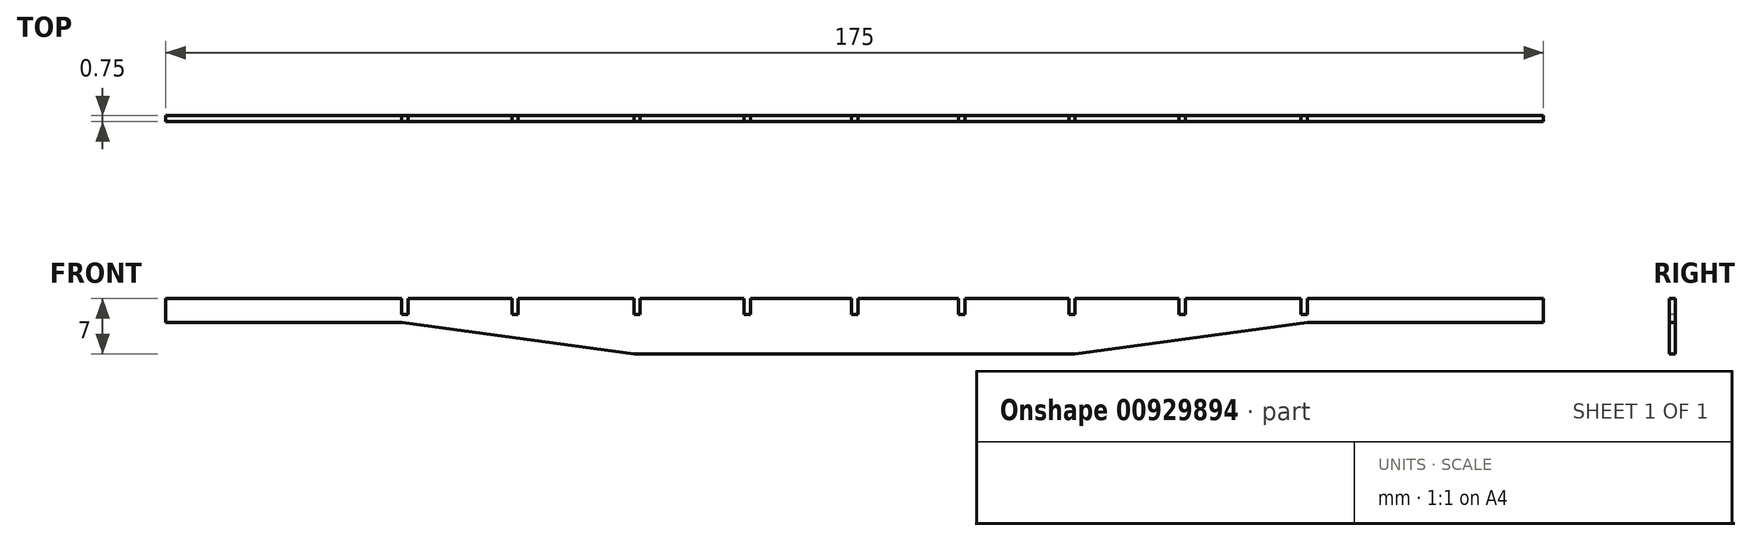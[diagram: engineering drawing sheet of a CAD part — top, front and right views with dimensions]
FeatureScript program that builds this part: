
annotation { "Feature Type Name" : "Feature", "Feature Type Description" : "" }
export const myFeature = defineFeature(function(context is Context, id is Id, definition is map)
    precondition{}
    {
        {
            var Q0;
            Q0=qCreatedBy(makeId("Front.planeOp"),FACE);
            var sketch = newSketch(context, id + "F0", { "sketchPlane" : qUnion([Q0])});
            skLineSegment(sketch, "E0", {"start": v(-85.02, 0) * mm, "end": v(-85.02, -3) * mm});
            skLineSegment(sketch, "E1", {"start": v(-85.02, -3) * mm, "end": v(-55.02, -3) * mm});
            skLineSegment(sketch, "E2", {"start": v(-55.02, -3) * mm, "end": v(-25.52, -7) * mm});
            skLineSegment(sketch, "E3", {"start": v(-25.52, -7) * mm, "end": v(30.48, -7) * mm});
            skLineSegment(sketch, "E4", {"start": v(30.48, -7) * mm, "end": v(59.98, -3) * mm});
            skLineSegment(sketch, "E5", {"start": v(59.98, -3) * mm, "end": v(89.98, -3) * mm});
            skLineSegment(sketch, "E6", {"start": v(89.98, -3) * mm, "end": v(89.98, 0) * mm});
            skLineSegment(sketch, "E7", {"start": v(89.98, 0) * mm, "end": v(-85.02, 0) * mm});
            skSolve(sketch);
        }
        {
            var Q0;
            Q0 = qSketchRegion(id + "F0", true);
            extrude(context, id + "F1", {"entities" : qUnion([Q0]), "depth" : .75 * mm, "offsetDistance" : 25 * mm});
        }
        {
            var Q0;
            Q0=makeQuery(id+"F1.opExtrude","CAP_FACE",FACE,{"disambiguationData":[OSD([sQuery(id+"F0.wireOp",EDGE,"E0"),sQuery(id+"F0.wireOp",EDGE,"E1"),sQuery(id+"F0.wireOp",EDGE,"E2"),sQuery(id+"F0.wireOp",EDGE,"E3"),sQuery(id+"F0.wireOp",EDGE,"E4"),sQuery(id+"F0.wireOp",EDGE,"E5"),sQuery(id+"F0.wireOp",EDGE,"E6"),sQuery(id+"F0.wireOp",EDGE,"E7")])],"isStart":false});
            var sketch = newSketch(context, id + "F2", { "sketchPlane" : qUnion([Q0])});
            skLineSegment(sketch, "E8", {"start": v(-55.04, 0) * mm, "end": v(-55.04, -2) * mm});
            skLineSegment(sketch, "E9", {"start": v(-55.04, -2) * mm, "end": v(-54.24, -2) * mm});
            skLineSegment(sketch, "E10", {"start": v(-54.24, -2) * mm, "end": v(-54.24, 0) * mm});
            skSolve(sketch);
        }
        {
            var Q0;
            Q0 = qSketchRegion(id + "F2", true);
            var Q1;
            {var subQ0=sQuery(id+"F2.wireOp",EDGE,"E8");Q1=makeQuery(id+"F2.imprint","IMPRINT",FACE,{"disambiguationData":[TD([[makeQuery(id+"F2.imprint","IMPRINT",EDGE,{"derivedFrom":subQ0}),1.0]])]});}
            extrude(context, id + "F3", {"entities" : qUnion([Q0, Q1]), "operationType" : NewBodyOperationType.REMOVE, "endBound" : BoundingType.THROUGH_ALL, "oppositeDirection" : true, "depth" : 25 * mm, "offsetDistance" : 25 * mm});
        }
        {
            var Q0;
            Q0=makeQuery(id+"F1.opExtrude","CAP_FACE",FACE,{"disambiguationData":[OSD([sQuery(id+"F0.wireOp",EDGE,"E0"),sQuery(id+"F0.wireOp",EDGE,"E1"),sQuery(id+"F0.wireOp",EDGE,"E2"),sQuery(id+"F0.wireOp",EDGE,"E3"),sQuery(id+"F0.wireOp",EDGE,"E4"),sQuery(id+"F0.wireOp",EDGE,"E5"),sQuery(id+"F0.wireOp",EDGE,"E6"),sQuery(id+"F0.wireOp",EDGE,"E7")])],"isStart":false});
            var sketch = newSketch(context, id + "F4", { "sketchPlane" : qUnion([Q0])});
            skLineSegment(sketch, "E11", {"start": v(-41.04, 0) * mm, "end": v(-41.04, -2) * mm});
            skLineSegment(sketch, "E12", {"start": v(-41.04, -2) * mm, "end": v(-40.24, -2) * mm});
            skLineSegment(sketch, "E13", {"start": v(-40.24, -2) * mm, "end": v(-40.24, 0) * mm});
            skSolve(sketch);
        }
        {
            var Q0;
            Q0 = qSketchRegion(id + "F4", true);
            var Q1;
            {var subQ0=sQuery(id+"F4.wireOp",EDGE,"E11");Q1=makeQuery(id+"F4.imprint","IMPRINT",FACE,{"disambiguationData":[TD([[makeQuery(id+"F4.imprint","IMPRINT",EDGE,{"derivedFrom":subQ0}),1.0]])]});}
            extrude(context, id + "F5", {"entities" : qUnion([Q0, Q1]), "operationType" : NewBodyOperationType.REMOVE, "endBound" : BoundingType.THROUGH_ALL, "oppositeDirection" : true, "depth" : 25 * mm, "offsetDistance" : 25 * mm});
        }
        {
            var Q0;
            Q0=makeQuery(id+"F1.opExtrude","CAP_FACE",FACE,{"disambiguationData":[OSD([sQuery(id+"F0.wireOp",EDGE,"E0"),sQuery(id+"F0.wireOp",EDGE,"E1"),sQuery(id+"F0.wireOp",EDGE,"E2"),sQuery(id+"F0.wireOp",EDGE,"E3"),sQuery(id+"F0.wireOp",EDGE,"E4"),sQuery(id+"F0.wireOp",EDGE,"E5"),sQuery(id+"F0.wireOp",EDGE,"E6"),sQuery(id+"F0.wireOp",EDGE,"E7")])],"isStart":false});
            var sketch = newSketch(context, id + "F6", { "sketchPlane" : qUnion([Q0])});
            skLineSegment(sketch, "E14", {"start": v(-25.54, 0) * mm, "end": v(-25.54, -2) * mm});
            skLineSegment(sketch, "E15", {"start": v(-25.54, -2) * mm, "end": v(-24.74, -2) * mm});
            skLineSegment(sketch, "E16", {"start": v(-24.74, -2) * mm, "end": v(-24.74, 0) * mm});
            skSolve(sketch);
        }
        {
            var Q0;
            Q0 = qSketchRegion(id + "F6", true);
            var Q1;
            {var subQ0=sQuery(id+"F6.wireOp",EDGE,"E14");Q1=makeQuery(id+"F6.imprint","IMPRINT",FACE,{"disambiguationData":[TD([[makeQuery(id+"F6.imprint","IMPRINT",EDGE,{"derivedFrom":subQ0}),1.0]])]});}
            extrude(context, id + "F7", {"entities" : qUnion([Q0, Q1]), "operationType" : NewBodyOperationType.REMOVE, "endBound" : BoundingType.THROUGH_ALL, "oppositeDirection" : true, "depth" : 25 * mm, "offsetDistance" : 25 * mm});
        }
        {
            var Q0;
            Q0=makeQuery(id+"F1.opExtrude","CAP_FACE",FACE,{"disambiguationData":[OSD([sQuery(id+"F0.wireOp",EDGE,"E0"),sQuery(id+"F0.wireOp",EDGE,"E1"),sQuery(id+"F0.wireOp",EDGE,"E2"),sQuery(id+"F0.wireOp",EDGE,"E3"),sQuery(id+"F0.wireOp",EDGE,"E4"),sQuery(id+"F0.wireOp",EDGE,"E5"),sQuery(id+"F0.wireOp",EDGE,"E6"),sQuery(id+"F0.wireOp",EDGE,"E7")])],"isStart":false});
            var sketch = newSketch(context, id + "F8", { "sketchPlane" : qUnion([Q0])});
            skLineSegment(sketch, "E17", {"start": v(-11.54, 0) * mm, "end": v(-11.54, -2) * mm});
            skLineSegment(sketch, "E18", {"start": v(-11.54, -2) * mm, "end": v(-10.74, -2) * mm});
            skLineSegment(sketch, "E19", {"start": v(-10.74, -2) * mm, "end": v(-10.74, 0) * mm});
            skSolve(sketch);
        }
        {
            var Q0;
            Q0 = qSketchRegion(id + "F8", true);
            var Q1;
            {var subQ0=sQuery(id+"F8.wireOp",EDGE,"E17");Q1=makeQuery(id+"F8.imprint","IMPRINT",FACE,{"disambiguationData":[TD([[makeQuery(id+"F8.imprint","IMPRINT",EDGE,{"derivedFrom":subQ0}),1.0]])]});}
            extrude(context, id + "F9", {"entities" : qUnion([Q0, Q1]), "operationType" : NewBodyOperationType.REMOVE, "endBound" : BoundingType.THROUGH_ALL, "oppositeDirection" : true, "depth" : 25 * mm, "offsetDistance" : 25 * mm});
        }
        {
            var Q0;
            Q0=makeQuery(id+"F1.opExtrude","CAP_FACE",FACE,{"disambiguationData":[OSD([sQuery(id+"F0.wireOp",EDGE,"E0"),sQuery(id+"F0.wireOp",EDGE,"E1"),sQuery(id+"F0.wireOp",EDGE,"E2"),sQuery(id+"F0.wireOp",EDGE,"E3"),sQuery(id+"F0.wireOp",EDGE,"E4"),sQuery(id+"F0.wireOp",EDGE,"E5"),sQuery(id+"F0.wireOp",EDGE,"E6"),sQuery(id+"F0.wireOp",EDGE,"E7")])],"isStart":false});
            var sketch = newSketch(context, id + "F10", { "sketchPlane" : qUnion([Q0])});
            skLineSegment(sketch, "E20", {"start": v(2.1, 0) * mm, "end": v(2.1, -2) * mm});
            skLineSegment(sketch, "E21", {"start": v(2.1, -2) * mm, "end": v(2.9, -2) * mm});
            skLineSegment(sketch, "E22", {"start": v(2.9, -2) * mm, "end": v(2.9, 0) * mm});
            skSolve(sketch);
        }
        {
            var Q0;
            Q0 = qSketchRegion(id + "F10", true);
            var Q1;
            {var subQ0=sQuery(id+"F10.wireOp",EDGE,"E20");Q1=makeQuery(id+"F10.imprint","IMPRINT",FACE,{"disambiguationData":[TD([[makeQuery(id+"F10.imprint","IMPRINT",EDGE,{"derivedFrom":subQ0}),1.0]])]});}
            extrude(context, id + "F11", {"entities" : qUnion([Q0, Q1]), "operationType" : NewBodyOperationType.REMOVE, "endBound" : BoundingType.THROUGH_ALL, "oppositeDirection" : true, "depth" : 25 * mm, "offsetDistance" : 25 * mm});
        }
        {
            var Q0;
            Q0=makeQuery(id+"F1.opExtrude","CAP_FACE",FACE,{"disambiguationData":[OSD([sQuery(id+"F0.wireOp",EDGE,"E0"),sQuery(id+"F0.wireOp",EDGE,"E1"),sQuery(id+"F0.wireOp",EDGE,"E2"),sQuery(id+"F0.wireOp",EDGE,"E3"),sQuery(id+"F0.wireOp",EDGE,"E4"),sQuery(id+"F0.wireOp",EDGE,"E5"),sQuery(id+"F0.wireOp",EDGE,"E6"),sQuery(id+"F0.wireOp",EDGE,"E7")])],"isStart":false});
            var sketch = newSketch(context, id + "F12", { "sketchPlane" : qUnion([Q0])});
            skLineSegment(sketch, "E23", {"start": v(15.7, 0) * mm, "end": v(15.7, -2) * mm});
            skLineSegment(sketch, "E24", {"start": v(15.7, -2) * mm, "end": v(16.5, -2) * mm});
            skLineSegment(sketch, "E25", {"start": v(16.5, -2) * mm, "end": v(16.5, 0) * mm});
            skSolve(sketch);
        }
        {
            var Q0;
            Q0 = qSketchRegion(id + "F12", true);
            var Q1;
            {var subQ0=sQuery(id+"F12.wireOp",EDGE,"E23");Q1=makeQuery(id+"F12.imprint","IMPRINT",FACE,{"disambiguationData":[TD([[makeQuery(id+"F12.imprint","IMPRINT",EDGE,{"derivedFrom":subQ0}),1.0]])]});}
            extrude(context, id + "F13", {"entities" : qUnion([Q0, Q1]), "operationType" : NewBodyOperationType.REMOVE, "endBound" : BoundingType.THROUGH_ALL, "oppositeDirection" : true, "depth" : 25 * mm, "offsetDistance" : 25 * mm});
        }
        {
            var Q0;
            Q0=makeQuery(id+"F1.opExtrude","CAP_FACE",FACE,{"disambiguationData":[OSD([sQuery(id+"F0.wireOp",EDGE,"E0"),sQuery(id+"F0.wireOp",EDGE,"E1"),sQuery(id+"F0.wireOp",EDGE,"E2"),sQuery(id+"F0.wireOp",EDGE,"E3"),sQuery(id+"F0.wireOp",EDGE,"E4"),sQuery(id+"F0.wireOp",EDGE,"E5"),sQuery(id+"F0.wireOp",EDGE,"E6"),sQuery(id+"F0.wireOp",EDGE,"E7")])],"isStart":false});
            var sketch = newSketch(context, id + "F14", { "sketchPlane" : qUnion([Q0])});
            skLineSegment(sketch, "E26", {"start": v(29.7, 0) * mm, "end": v(29.7, -2) * mm});
            skLineSegment(sketch, "E27", {"start": v(29.7, -2) * mm, "end": v(30.5, -2) * mm});
            skLineSegment(sketch, "E28", {"start": v(30.5, -2) * mm, "end": v(30.5, 0) * mm});
            skSolve(sketch);
        }
        {
            var Q0;
            Q0 = qSketchRegion(id + "F14", true);
            var Q1;
            {var subQ0=sQuery(id+"F14.wireOp",EDGE,"E26");Q1=makeQuery(id+"F14.imprint","IMPRINT",FACE,{"disambiguationData":[TD([[makeQuery(id+"F14.imprint","IMPRINT",EDGE,{"derivedFrom":subQ0}),1.0]])]});}
            extrude(context, id + "F15", {"entities" : qUnion([Q0, Q1]), "operationType" : NewBodyOperationType.REMOVE, "endBound" : BoundingType.THROUGH_ALL, "oppositeDirection" : true, "depth" : 25 * mm, "offsetDistance" : 25 * mm});
        }
        {
            var Q0;
            Q0=makeQuery(id+"F1.opExtrude","CAP_FACE",FACE,{"disambiguationData":[OSD([sQuery(id+"F0.wireOp",EDGE,"E0"),sQuery(id+"F0.wireOp",EDGE,"E1"),sQuery(id+"F0.wireOp",EDGE,"E2"),sQuery(id+"F0.wireOp",EDGE,"E3"),sQuery(id+"F0.wireOp",EDGE,"E4"),sQuery(id+"F0.wireOp",EDGE,"E5"),sQuery(id+"F0.wireOp",EDGE,"E6"),sQuery(id+"F0.wireOp",EDGE,"E7")])],"isStart":false});
            var sketch = newSketch(context, id + "F16", { "sketchPlane" : qUnion([Q0])});
            skLineSegment(sketch, "E29", {"start": v(43.7, 0) * mm, "end": v(43.7, -2) * mm});
            skLineSegment(sketch, "E30", {"start": v(43.7, -2) * mm, "end": v(44.5, -2) * mm});
            skLineSegment(sketch, "E31", {"start": v(44.5, -2) * mm, "end": v(44.5, 0) * mm});
            skSolve(sketch);
        }
        {
            var Q0;
            Q0 = qSketchRegion(id + "F16", true);
            var Q1;
            {var subQ0=sQuery(id+"F16.wireOp",EDGE,"E29");Q1=makeQuery(id+"F16.imprint","IMPRINT",FACE,{"disambiguationData":[TD([[makeQuery(id+"F16.imprint","IMPRINT",EDGE,{"derivedFrom":subQ0}),1.0]])]});}
            extrude(context, id + "F17", {"entities" : qUnion([Q0, Q1]), "operationType" : NewBodyOperationType.REMOVE, "endBound" : BoundingType.THROUGH_ALL, "oppositeDirection" : true, "depth" : 25 * mm, "offsetDistance" : 25 * mm});
        }
        {
            var Q0;
            Q0=makeQuery(id+"F1.opExtrude","CAP_FACE",FACE,{"disambiguationData":[OSD([sQuery(id+"F0.wireOp",EDGE,"E0"),sQuery(id+"F0.wireOp",EDGE,"E1"),sQuery(id+"F0.wireOp",EDGE,"E2"),sQuery(id+"F0.wireOp",EDGE,"E3"),sQuery(id+"F0.wireOp",EDGE,"E4"),sQuery(id+"F0.wireOp",EDGE,"E5"),sQuery(id+"F0.wireOp",EDGE,"E6"),sQuery(id+"F0.wireOp",EDGE,"E7")])],"isStart":false});
            var sketch = newSketch(context, id + "F18", { "sketchPlane" : qUnion([Q0])});
            skLineSegment(sketch, "E32", {"start": v(59.2, 0) * mm, "end": v(59.2, -2) * mm});
            skLineSegment(sketch, "E33", {"start": v(59.2, -2) * mm, "end": v(60, -2) * mm});
            skLineSegment(sketch, "E34", {"start": v(60, -2) * mm, "end": v(60, 0) * mm});
            skSolve(sketch);
        }
        {
            var Q0;
            Q0 = qSketchRegion(id + "F18", true);
            var Q1;
            {var subQ0=sQuery(id+"F18.wireOp",EDGE,"E32");Q1=makeQuery(id+"F18.imprint","IMPRINT",FACE,{"disambiguationData":[TD([[makeQuery(id+"F18.imprint","IMPRINT",EDGE,{"derivedFrom":subQ0}),1.0]])]});}
            extrude(context, id + "F19", {"entities" : qUnion([Q0, Q1]), "operationType" : NewBodyOperationType.REMOVE, "endBound" : BoundingType.THROUGH_ALL, "oppositeDirection" : true, "depth" : 25 * mm, "offsetDistance" : 25 * mm});
        }
    });
